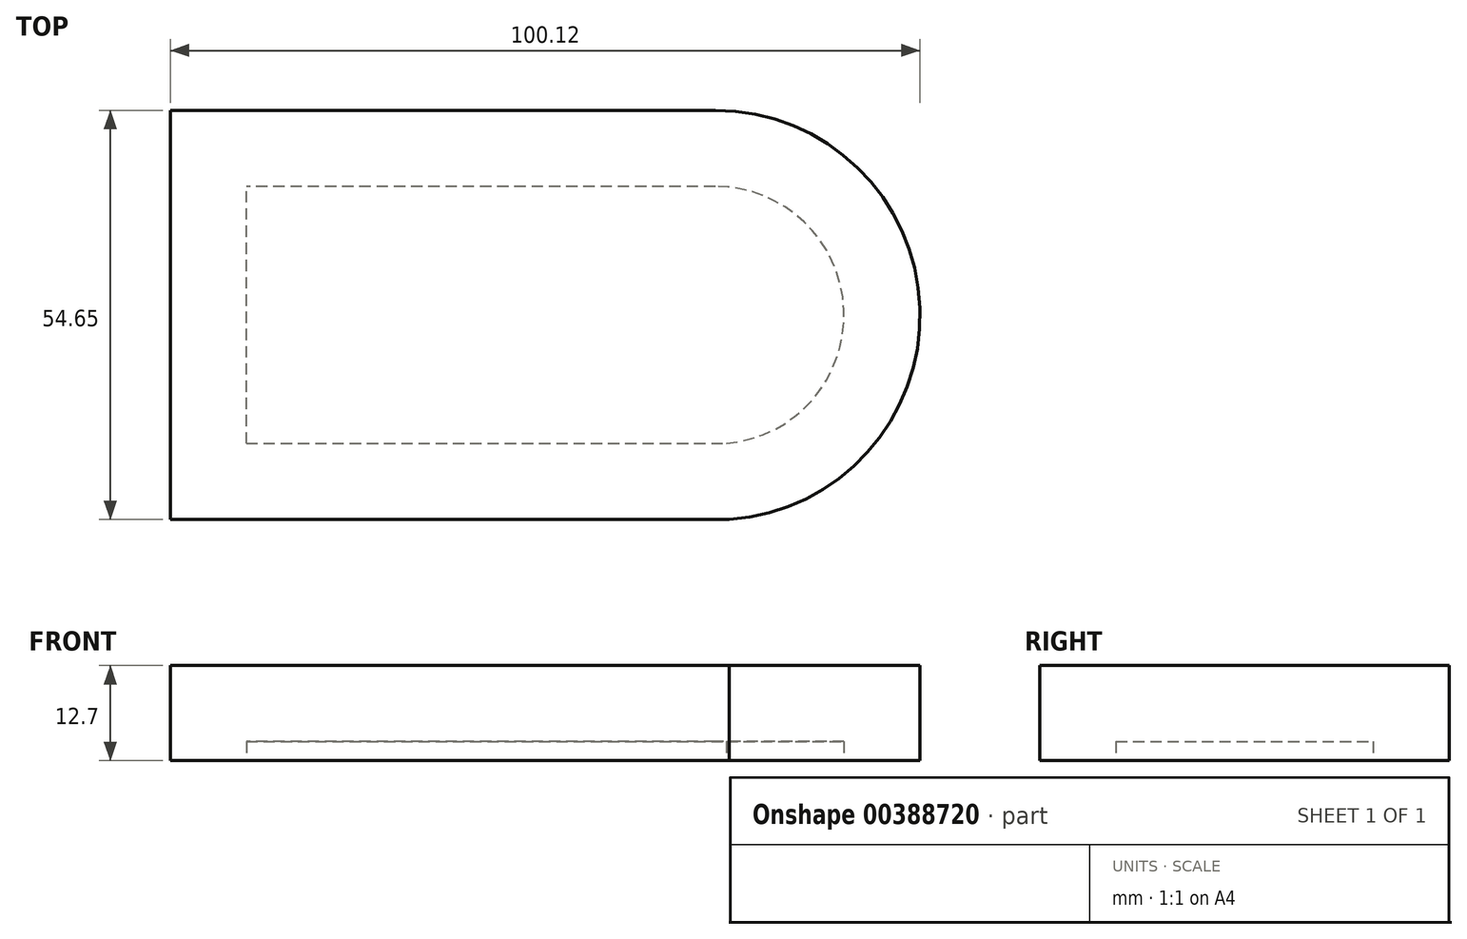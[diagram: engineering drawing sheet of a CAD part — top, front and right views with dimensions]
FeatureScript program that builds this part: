
annotation { "Feature Type Name" : "Feature", "Feature Type Description" : "" }
export const myFeature = defineFeature(function(context is Context, id is Id, definition is map)
    precondition{}
    {
        {
            var Q0;
            Q0=qCreatedBy(makeId("Top.planeOp"),FACE);
            var sketch = newSketch(context, id + "F0", { "sketchPlane" : qUnion([Q0])});
            skLineSegment(sketch, "E0", {"start": v(-49.05, -28.57) * mm, "end": v(-49.05, 26.08) * mm});
            skLineSegment(sketch, "E1", {"start": v(-49.05, 26.08) * mm, "end": v(-49.05, 26.08) * mm});
            skLineSegment(sketch, "E2", {"start": v(23.72, 26.08) * mm, "end": v(-49.05, 26.08) * mm});
            skLineSegment(sketch, "E3", {"start": v(-49.05, -28.57) * mm, "end": v(25.6, -28.57) * mm});
            skLineSegment(sketch, "E4", {"start": v(25.6, -28.57) * mm, "end": v(25.6, -28.57) * mm});
            skArc(sketch, "E5", {"start": v(25.6, -28.57) * mm, "mid": v(51.06, -0.34) * mm, "end": v(23.72, 26.08) * mm});
            skSolve(sketch);
        }
        {
            var Q0;
            Q0=makeQuery(id+"F0.imprint","IMPRINT",FACE,{"disambiguationData":[TD([[makeQuery(id+"F0.imprint","IMPRINT",EDGE,{"derivedFrom":sQuery(id+"F0.wireOp",EDGE,"E0")}),-1.0]])]});
            extrude(context, id + "F1", {"entities" : qUnion([Q0]), "depth" : 12.7 * mm});
        }
        {
            var Q0;
            Q0=makeQuery(id+"F1.opExtrude","CAP_FACE",FACE,{"disambiguationData":[OSD([sQuery(id+"F0.wireOp",EDGE,"E0"),sQuery(id+"F0.wireOp",EDGE,"E2"),sQuery(id+"F0.wireOp",EDGE,"E3"),sQuery(id+"F0.wireOp",EDGE,"E5")])],"isStart":true});
            shell(context, id + "F2", {"entities" : qUnion([Q0]), "thickness" : 10.16 * mm});
        }
    });
